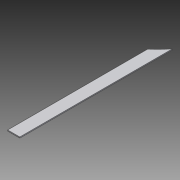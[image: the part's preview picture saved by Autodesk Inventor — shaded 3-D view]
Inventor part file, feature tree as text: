
AUTODESK INVENTOR PART (.ipt)
format: ipt  version: 2014 SP1 (Build 180222100, 222)  size: 74,752 bytes
history: native  units: in
note: dims shown in document units (in); Inventor stores cm internally (conversion verified against a paired STEP export)
features: extrude x1, sketch x1
ambient origin geometry x8: Origin, YZ Plane, XZ Plane, XY Plane, X Axis, Y Axis, Z Axis, Center Point
bodies: Solid1 (feature_tree)
feature tree (2):
  extrude  "Extrusion1"  Depth=0.0625in
  sketch  "Sketch1"  dims[d0=11.5in d1=13.0in d2=13.0in d3=0.75in d7=1.25in d11=0.0625in d12=0.0in]
